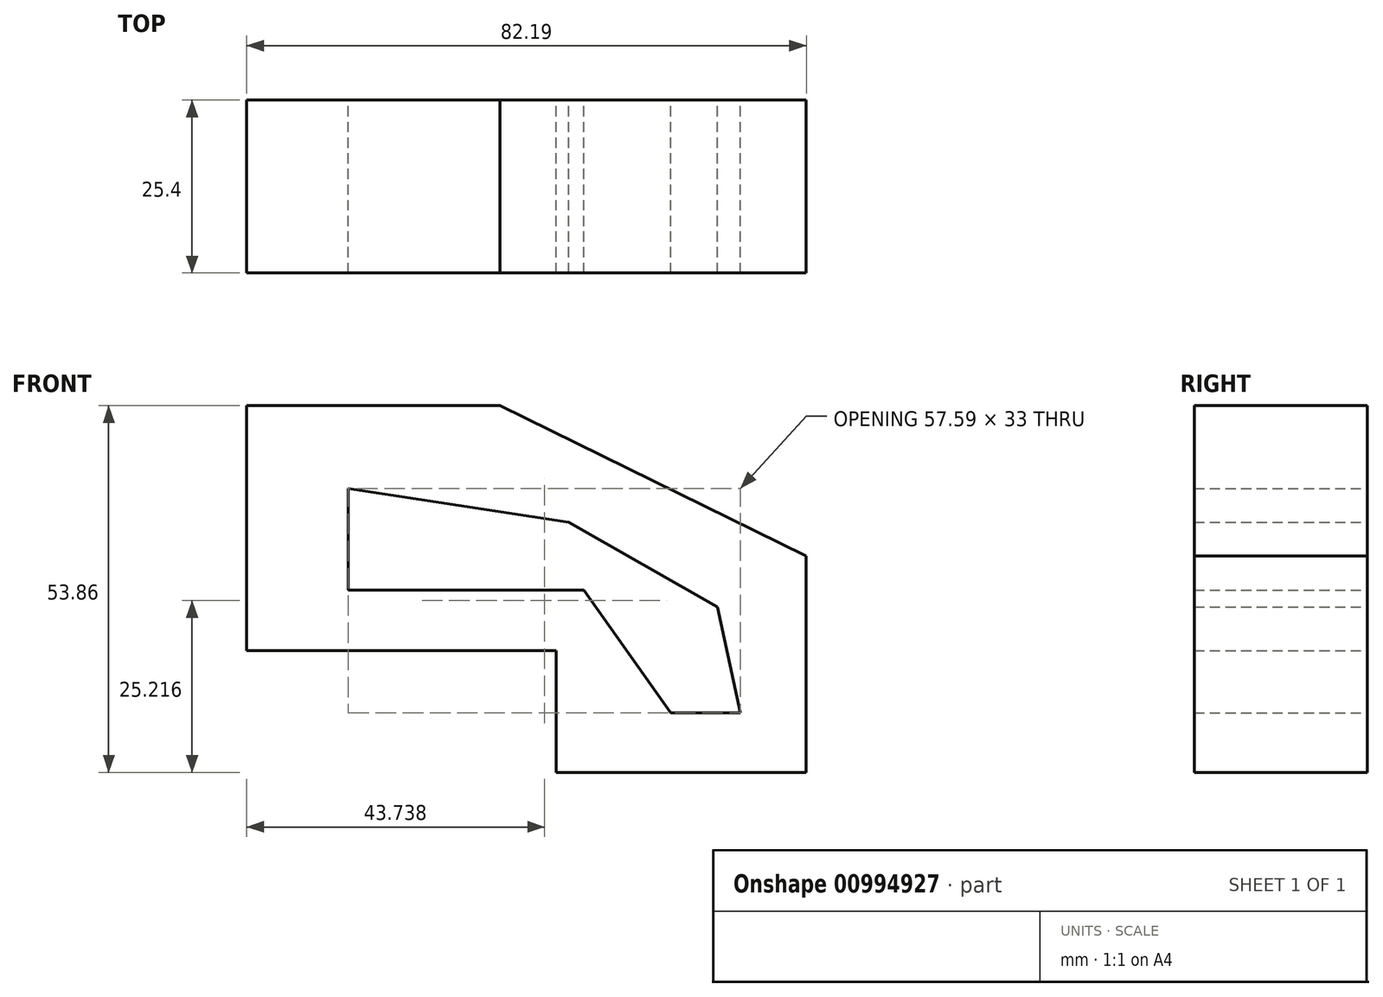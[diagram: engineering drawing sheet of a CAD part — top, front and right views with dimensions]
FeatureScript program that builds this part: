
annotation { "Feature Type Name" : "Feature", "Feature Type Description" : "" }
export const myFeature = defineFeature(function(context is Context, id is Id, definition is map)
    precondition{}
    {
        {
            var Q0;
            Q0=qCreatedBy(makeId("Front.planeOp"),FACE);
            var sketch = newSketch(context, id + "F0", { "sketchPlane" : qUnion([Q0])});
            skLineSegment(sketch, "E0", {"start": v(0, 0) * mm, "end": v(-37.2, 0) * mm});
            skLineSegment(sketch, "E1", {"start": v(-37.2, 0) * mm, "end": v(-37.2, 35.96) * mm});
            skLineSegment(sketch, "E2", {"start": v(-37.2, 35.96) * mm, "end": v(0, 35.96) * mm});
            skLineSegment(sketch, "E3", {"start": v(0, 35.96) * mm, "end": v(44.99, 13.85) * mm});
            skLineSegment(sketch, "E4", {"start": v(44.99, 13.85) * mm, "end": v(44.99, -17.9) * mm});
            skLineSegment(sketch, "E5", {"start": v(44.99, -17.9) * mm, "end": v(8.25, -17.9) * mm});
            skLineSegment(sketch, "E6", {"start": v(8.25, -17.9) * mm, "end": v(8.25, 0) * mm});
            skLineSegment(sketch, "E7", {"start": v(8.25, 0) * mm, "end": v(0, 0) * mm});
            skLineSegment(sketch, "E8", {"start": v(-22.26, 23.82) * mm, "end": v(-22.26, 8.87) * mm});
            skLineSegment(sketch, "E9", {"start": v(-22.26, 8.87) * mm, "end": v(12.3, 8.87) * mm});
            skLineSegment(sketch, "E10", {"start": v(12.3, 8.87) * mm, "end": v(25.06, -9.18) * mm});
            skLineSegment(sketch, "E11", {"start": v(25.06, -9.18) * mm, "end": v(35.34, -9.18) * mm});
            skLineSegment(sketch, "E12", {"start": v(35.34, -9.18) * mm, "end": v(31.91, 6.38) * mm});
            skLineSegment(sketch, "E13", {"start": v(31.91, 6.38) * mm, "end": v(10.12, 18.84) * mm});
            skLineSegment(sketch, "E14", {"start": v(10.12, 18.84) * mm, "end": v(-22.26, 23.82) * mm});
            skSolve(sketch);
        }
        {
            var Q0;
            Q0=makeQuery(id+"F0.imprint","IMPRINT",FACE,{"disambiguationData":[TD([[makeQuery(id+"F0.imprint","IMPRINT",EDGE,{"derivedFrom":sQuery(id+"F0.wireOp",EDGE,"E0")}),-1.0]])]});
            extrude(context, id + "F1", {"entities" : qUnion([Q0]), "endBound" : BoundingType.SYMMETRIC, "depth" : 25.4 * mm, "offsetDistance" : 25.4 * mm});
        }
    });
